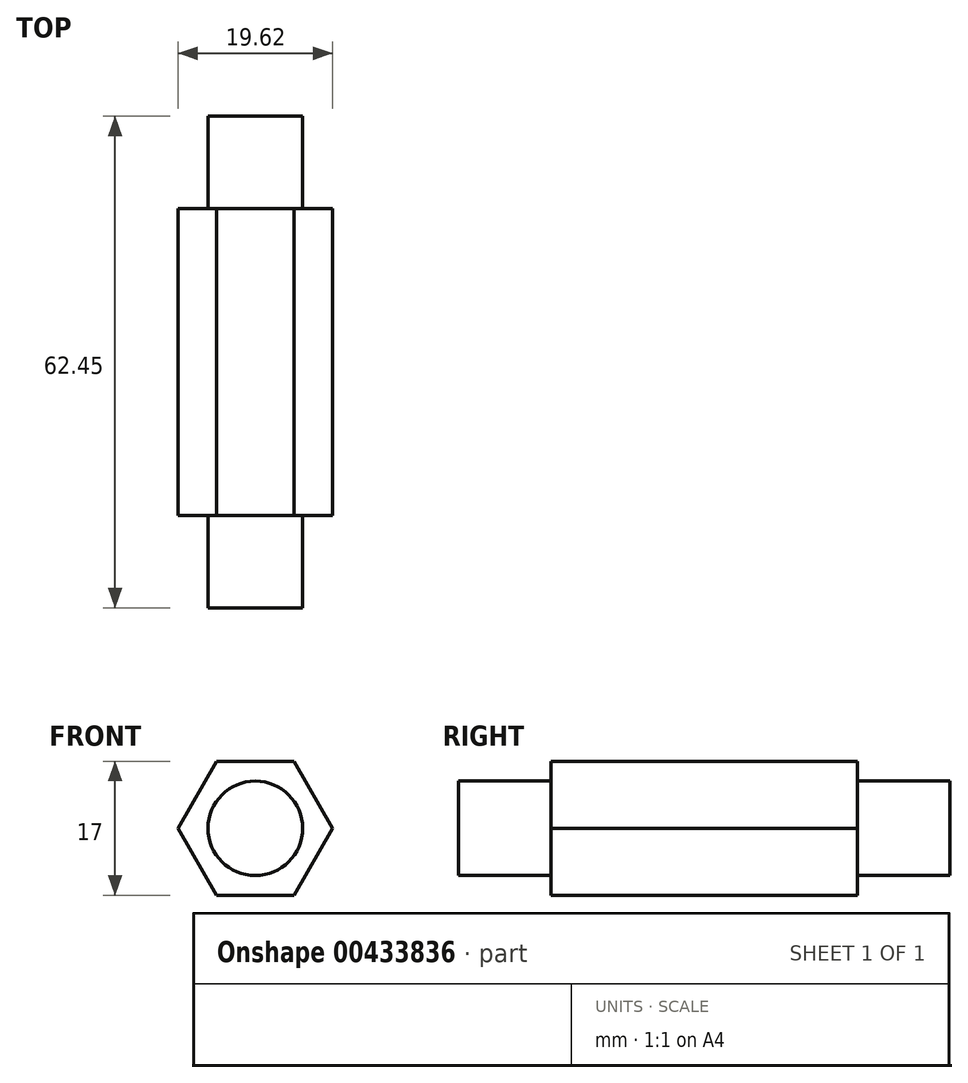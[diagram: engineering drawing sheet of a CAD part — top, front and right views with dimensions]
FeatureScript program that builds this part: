
annotation { "Feature Type Name" : "Feature", "Feature Type Description" : "" }
export const myFeature = defineFeature(function(context is Context, id is Id, definition is map)
    precondition{}
    {
        {
            var Q0;
            Q0=qCreatedBy(makeId("Front.planeOp"),FACE);
            var sketch = newSketch(context, id + "F0", { "sketchPlane" : qUnion([Q0])});
            skCircle(sketch, "E0.cCircle", {"center": v(0, 0) * mm, "radius": 8.5 * mm, "construction": true});
            skLineSegment(sketch, "E0.0", {"start": v(4.9, -8.5) * mm, "end": v(-4.9, -8.5) * mm});
            skLineSegment(sketch, "E0.1", {"start": v(-4.9, -8.5) * mm, "end": v(-9.81, 0) * mm});
            skLineSegment(sketch, "E0.2", {"start": v(-9.81, 0) * mm, "end": v(-4.9, 8.5) * mm});
            skLineSegment(sketch, "E0.3", {"start": v(-4.9, 8.5) * mm, "end": v(4.9, 8.5) * mm});
            skLineSegment(sketch, "E0.4", {"start": v(4.9, 8.5) * mm, "end": v(9.81, 0) * mm});
            skLineSegment(sketch, "E0.5", {"start": v(9.81, 0) * mm, "end": v(4.9, -8.5) * mm});
            skPoint(sketch, "E0.0.midPoint", {"position": v(0, -8.5) * mm});
            skSolve(sketch);
        }
        {
            var Q0;
            Q0 = qSketchRegion(id + "F0", true);
            extrude(context, id + "F1", {"entities" : qUnion([Q0]), "oppositeDirection" : true, "depth" : 62.45 * mm});
        }
        {
            var Q0;
            Q0=makeQuery(id+"F1.opExtrude","CAP_FACE",FACE,{"disambiguationData":[OSD([sQuery(id+"F0.wireOp",EDGE,"E0.0"),sQuery(id+"F0.wireOp",EDGE,"E0.1"),sQuery(id+"F0.wireOp",EDGE,"E0.2"),sQuery(id+"F0.wireOp",EDGE,"E0.3"),sQuery(id+"F0.wireOp",EDGE,"E0.4"),sQuery(id+"F0.wireOp",EDGE,"E0.5")])],"isStart":true});
            var sketch = newSketch(context, id + "F2", { "sketchPlane" : qUnion([Q0])});
            skCircle(sketch, "E1", {"center": v(0, 0) * mm, "radius": 16.48 * mm});
            skCircle(sketch, "E2", {"center": v(0, 0) * mm, "radius": 6 * mm});
            skSolve(sketch);
        }
        {
            var Q0;
            Q0 = qSketchRegion(id + "F2", true);
            extrude(context, id + "F3", {"entities" : qUnion([Q0]), "operationType" : NewBodyOperationType.REMOVE, "oppositeDirection" : true, "depth" : 11.75 * mm});
        }
        {
            var Q0;
            Q0=makeQuery(id+"F1.opExtrude","CAP_FACE",FACE,{"disambiguationData":[OSD([sQuery(id+"F0.wireOp",EDGE,"E0.0"),sQuery(id+"F0.wireOp",EDGE,"E0.1"),sQuery(id+"F0.wireOp",EDGE,"E0.2"),sQuery(id+"F0.wireOp",EDGE,"E0.3"),sQuery(id+"F0.wireOp",EDGE,"E0.4"),sQuery(id+"F0.wireOp",EDGE,"E0.5")])],"isStart":false});
            var sketch = newSketch(context, id + "F4", { "sketchPlane" : qUnion([Q0])});
            skCircle(sketch, "E3", {"center": v(0, 0) * mm, "radius": 15.41 * mm});
            skCircle(sketch, "E4", {"center": v(0, 0) * mm, "radius": 6 * mm});
            skSolve(sketch);
        }
        {
            var Q0;
            Q0 = qSketchRegion(id + "F4", true);
            extrude(context, id + "F5", {"entities" : qUnion([Q0]), "operationType" : NewBodyOperationType.REMOVE, "oppositeDirection" : true, "depth" : 11.75 * mm});
        }
    });
